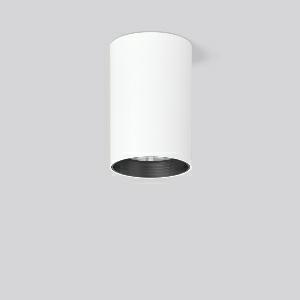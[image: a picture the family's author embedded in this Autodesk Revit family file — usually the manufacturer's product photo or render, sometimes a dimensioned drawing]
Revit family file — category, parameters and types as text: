
# Revit family: heledon_maxi_a_931220_002_2_76_2750
name_source: partatom
category: Lighting Fixtures
units: mm (PartAtom-declared; Revit-internal decimal feet)

## family parameters
Cut with Voids When Loaded = No
Host = Face
Light Source = No
Part Type = Normal
Room Calculation Point = No
Round Connector Dimension = Use Diameter
Shared = No

## types (1)
- HELEDON maxi A (1 x LED Modul 927, 2650 lm, 2700)
    Apparent Load = 25 VA
    Approval mark = CE
    CIE Flux Codes = 97 100 100 100 100
    Color Rendering = 92
    Color Temperature = 2700
    Default Elevation = 1800 mm
    Description = Series: HELEDON maxi
Cylindrical surface-mounted downlight. Housing: die-cast aluminium, powder-coated. Internal ceiling frame polycarbonate with bayonet mounting. Black plastic ring and recessed LED to prevent glare from the side. Optical assembly with lens made of plastic (polycarbonate) for the best homogeneous light distribution - can be changed without tools. Best colour rendering index Ra>90. Suitable for Ceiling mounting. Easy installation with a separate ceiling frame with bayonet mounting and plug connection. Driver integrated. Connected via plug-in connector. High quality converter without flickering and stroboscopic effect. The following accessories can be mounted without use of tools: interchangeable lenses, decorative glasses, honeycomb louvre, clear and frosted diffusers, white interchangeable plastic ring. 
Colour: traffic white, matt (RAL 9016)
Diameter: 123 mm
Height: 183 mm
Lamp: LED
Socket: without socket
Colour temperature: 2700K
Colour rendering index (CRI): 92
System power: 25 W
Rated luminous flux: 2650 lm
Luminous efficiency: 106 lm/W
Control gear: Converter, dimmable, DALI
Protection class: I
Type of protection: IP 20
    Height = 183 mm
    Lamp = 1 x LED Modul 927
    Lamp Light Flux = 2650 lm
    Lamp count = 1
    Length = 123 mm
    Lifetime = 50000 h
    Luminous efficacy = 106 lm/W
    Manufacturer = RZB
    ModVariant = No
    Model = 931220.002.2.76
    Mounting Place = Ceiling
    Mounting Type = Surface mounted
    Number of Poles = 1
    OnlyDefault = Yes
    Power Factor = 1
    Product Name = HELEDON maxi A
    Product group = Surface mounted downlights
    ProductGroupID = 302
    Protection Class = Protection class I
    Protection Degree = IP 20
    RLX_Detail_Level = 1
    RLX_Emergency_Light_Flux = 0 lm
    RLX_Emergency_Type = 0
    RLX_Emergency_Type_DB = No
    RlxData = <blob elided: 99489 chars, md5=187308a8>
    Socket = socket
    Standby Power = 0 W
    System Light Flux = 2650 lm
    System Power = 25 W
    Type Comments = Product without accessories
    Type Image = 931193.002.jpg
    URL = http://relux.com
    VarID = ---
    Voltage = 230 V
    Voltage Range = 220-240 V
    Weight = 0.00 kg
    Width = 0 mm  [stored 0 ft]

note: [stored X ft] marks values corroborated as IEEE doubles in the binary element streams (Revit-internal decimal feet)

## geometry (parser evidence)
native form markers: Blend x4, Sweep x10
no freeform markers — native parametric forms only
